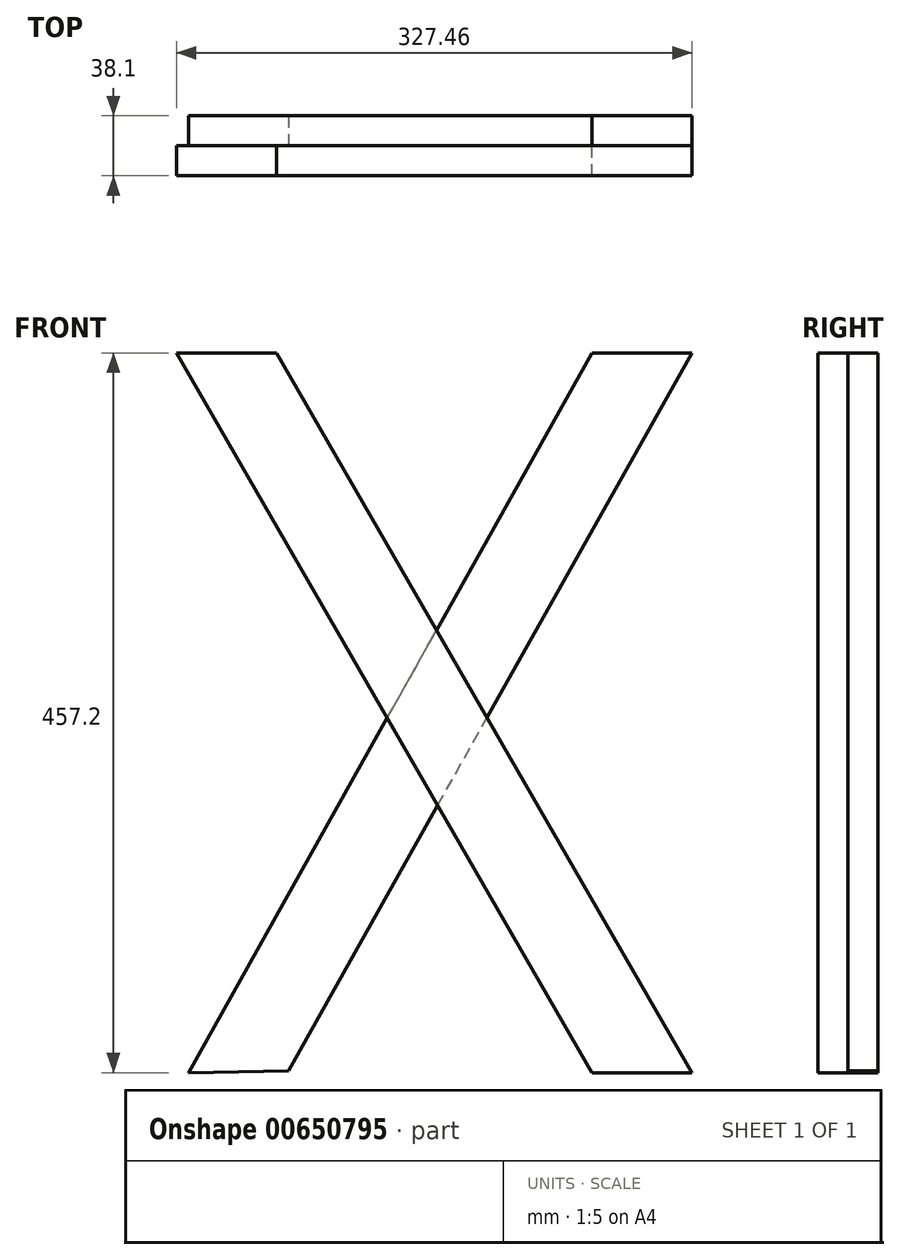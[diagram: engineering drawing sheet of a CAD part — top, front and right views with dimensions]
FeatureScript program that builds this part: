
annotation { "Feature Type Name" : "Feature", "Feature Type Description" : "" }
export const myFeature = defineFeature(function(context is Context, id is Id, definition is map)
    precondition{}
    {
        {
            var Q0;
            Q0=qCreatedBy(makeId("Front.planeOp"),FACE);
            var sketch = newSketch(context, id + "F0", { "sketchPlane" : qUnion([Q0])});
            skLineSegment(sketch, "E0", {"start": v(0, 0) * mm, "end": v(0, 457.2) * mm});
            skLineSegment(sketch, "E1", {"start": v(0, 0) * mm, "end": v(-263.96, 457.2) * mm});
            skLineSegment(sketch, "E2", {"start": v(-263.96, 457.2) * mm, "end": v(-327.46, 457.2) * mm});
            skLineSegment(sketch, "E3", {"start": v(0, 0) * mm, "end": v(-63.5, 0) * mm});
            skLineSegment(sketch, "E4", {"start": v(-63.5, 0) * mm, "end": v(-327.46, 457.2) * mm});
            skSolve(sketch);
        }
        {
            var Q0;
            Q0=makeQuery(id+"F0.imprint","IMPRINT",FACE,{"disambiguationData":[TD([[makeQuery(id+"F0.imprint","IMPRINT",EDGE,{"derivedFrom":sQuery(id+"F0.wireOp",EDGE,"E1")}),1.0]])]});
            extrude(context, id + "F1", {"entities" : qUnion([Q0]), "depth" : 19.05 * mm, "offsetDistance" : 25.4 * mm});
        }
        {
            var Q0;
            Q0=makeQuery(id+"F1.opExtrude","CAP_FACE",FACE,{"disambiguationData":[OSD([sQuery(id+"F0.wireOp",EDGE,"E1"),sQuery(id+"F0.wireOp",EDGE,"E2"),sQuery(id+"F0.wireOp",EDGE,"E3"),sQuery(id+"F0.wireOp",EDGE,"E4")])],"isStart":true});
            var sketch = newSketch(context, id + "F2", { "sketchPlane" : qUnion([Q0])});
            skLineSegment(sketch, "E5", {"start": v(327.46, 457.2) * mm, "end": v(319.71, 0) * mm});
            skLineSegment(sketch, "E6", {"start": v(319.71, 0) * mm, "end": v(63.5, 457.2) * mm});
            skLineSegment(sketch, "E7", {"start": v(63.5, 457.2) * mm, "end": v(0, 457.2) * mm});
            skLineSegment(sketch, "E8", {"start": v(319.71, 0) * mm, "end": v(256.22, 1.08) * mm});
            skLineSegment(sketch, "E9", {"start": v(256.22, 1.08) * mm, "end": v(0, 457.2) * mm});
            skSolve(sketch);
        }
        {
            var Q0;
            {var subQ0=sQuery(id+"F2.wireOp",EDGE,"E7");Q0=makeQuery(id+"F2.imprint","IMPRINT",FACE,{"disambiguationData":[TD([[makeQuery(id+"F2.imprint","IMPRINT",EDGE,{"derivedFrom":subQ0}),1.0]])]});}
            var Q1;
            {var subQ0=sQuery(id+"F2.wireOp",EDGE,"E6");var subQ1=makeQuery(id+"F1.opExtrude","CAP_EDGE",EDGE,{"disambiguationData":[OSD([sQuery(id+"F0.wireOp",EDGE,"E1")])],"isStart":true});var subQ2=makeQuery(id+"F2.imprint","INTERSECT",VERTEX,{"derivedFrom":[subQ1,subQ0]});Q1=makeQuery(id+"F2.imprint","IMPRINT",FACE,{"disambiguationData":[TD([[makeQuery(id+"F2.imprint","IMPRINT",EDGE,{"disambiguationData":[TD([[subQ2,1.0]])],"derivedFrom":subQ0}),1.0]])]});}
            var Q2;
            {var subQ0=sQuery(id+"F2.wireOp",EDGE,"E8");Q2=makeQuery(id+"F2.imprint","IMPRINT",FACE,{"disambiguationData":[TD([[makeQuery(id+"F2.imprint","IMPRINT",EDGE,{"derivedFrom":subQ0}),-1.0]])]});}
            extrude(context, id + "F3", {"entities" : qUnion([Q0, Q1, Q2]), "operationType" : NewBodyOperationType.ADD, "depth" : 19.05 * mm, "offsetDistance" : 25.4 * mm});
        }
    });
